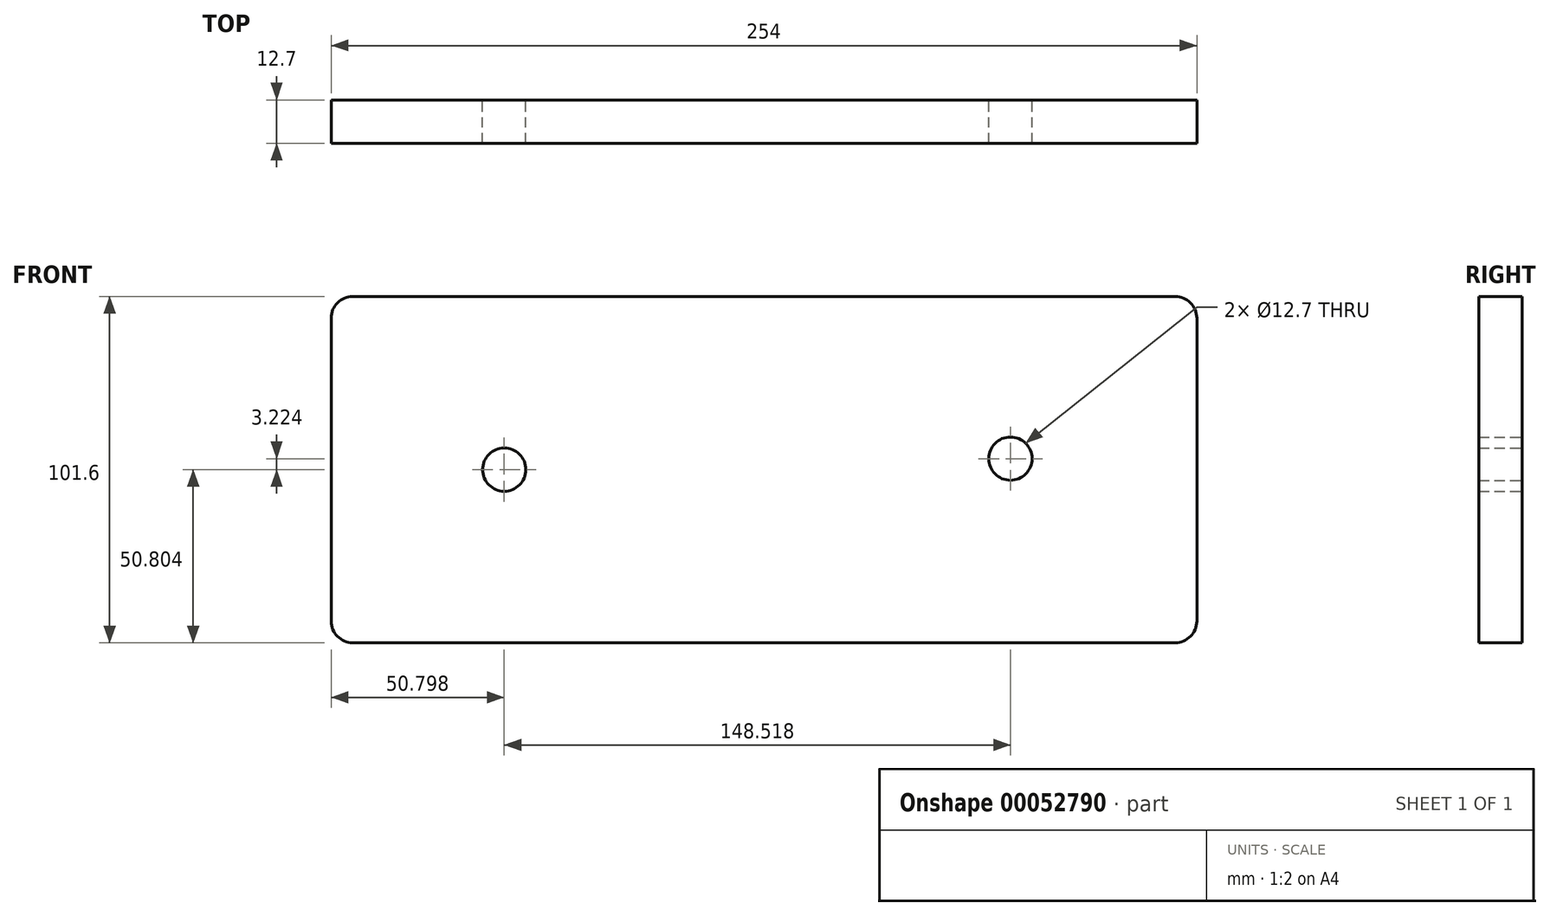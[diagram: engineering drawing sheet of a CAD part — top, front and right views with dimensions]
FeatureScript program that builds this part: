
annotation { "Feature Type Name" : "Feature", "Feature Type Description" : "" }
export const myFeature = defineFeature(function(context is Context, id is Id, definition is map)
    precondition{}
    {
        {
            var Q0;
            Q0=qCreatedBy(makeId("Front.planeOp"),FACE);
            var sketch = newSketch(context, id + "F0", { "sketchPlane" : qUnion([Q0])});
            skLineSegment(sketch, "E0.bottom", {"start": v(-126.01, 33.98) * mm, "end": v(127.99, 33.98) * mm});
            skLineSegment(sketch, "E0.top", {"start": v(-126.01, -67.62) * mm, "end": v(127.99, -67.62) * mm});
            skLineSegment(sketch, "E0.left", {"start": v(-126.01, 33.98) * mm, "end": v(-126.01, -67.62) * mm});
            skLineSegment(sketch, "E0.right", {"start": v(127.99, 33.98) * mm, "end": v(127.99, -67.62) * mm});
            skCircle(sketch, "E1", {"center": v(-75.21, -16.82) * mm, "radius": 6.35 * mm});
            skCircle(sketch, "E2", {"center": v(73.3, -13.6) * mm, "radius": 6.35 * mm});
            skSolve(sketch);
        }
        {
            var Q0;
            Q0 = qSketchRegion(id + "F0", true);
            extrude(context, id + "F1", {"entities" : qUnion([Q0]), "depth" : 12.7 * mm});
        }
        {
            var Q0;
            Q0=makeQuery(id+"F1.opExtrude","SWEPT_EDGE",EDGE,{"disambiguationData":[OSD([sQuery(id+"F0.wireOp",EDGE,"E0.top"),sQuery(id+"F0.wireOp",EDGE,"E0.left")])]});
            var Q1;
            Q1=makeQuery(id+"F1.opExtrude","SWEPT_EDGE",EDGE,{"disambiguationData":[OSD([sQuery(id+"F0.wireOp",EDGE,"E0.top"),sQuery(id+"F0.wireOp",EDGE,"E0.right")])]});
            var Q2;
            Q2=makeQuery(id+"F1.opExtrude","SWEPT_EDGE",EDGE,{"disambiguationData":[OSD([sQuery(id+"F0.wireOp",EDGE,"E0.bottom"),sQuery(id+"F0.wireOp",EDGE,"E0.right")])]});
            var Q3;
            Q3=makeQuery(id+"F1.opExtrude","SWEPT_EDGE",EDGE,{"disambiguationData":[OSD([sQuery(id+"F0.wireOp",EDGE,"E0.bottom"),sQuery(id+"F0.wireOp",EDGE,"E0.left")])]});
            fillet(context, id + "F2", {"entities" : qUnion([Q0, Q1, Q2, Q3]), "radius" : 6.35 * mm, "tangentPropagation" : true, "allowEdgeOverflow" : false});
        }
    });
